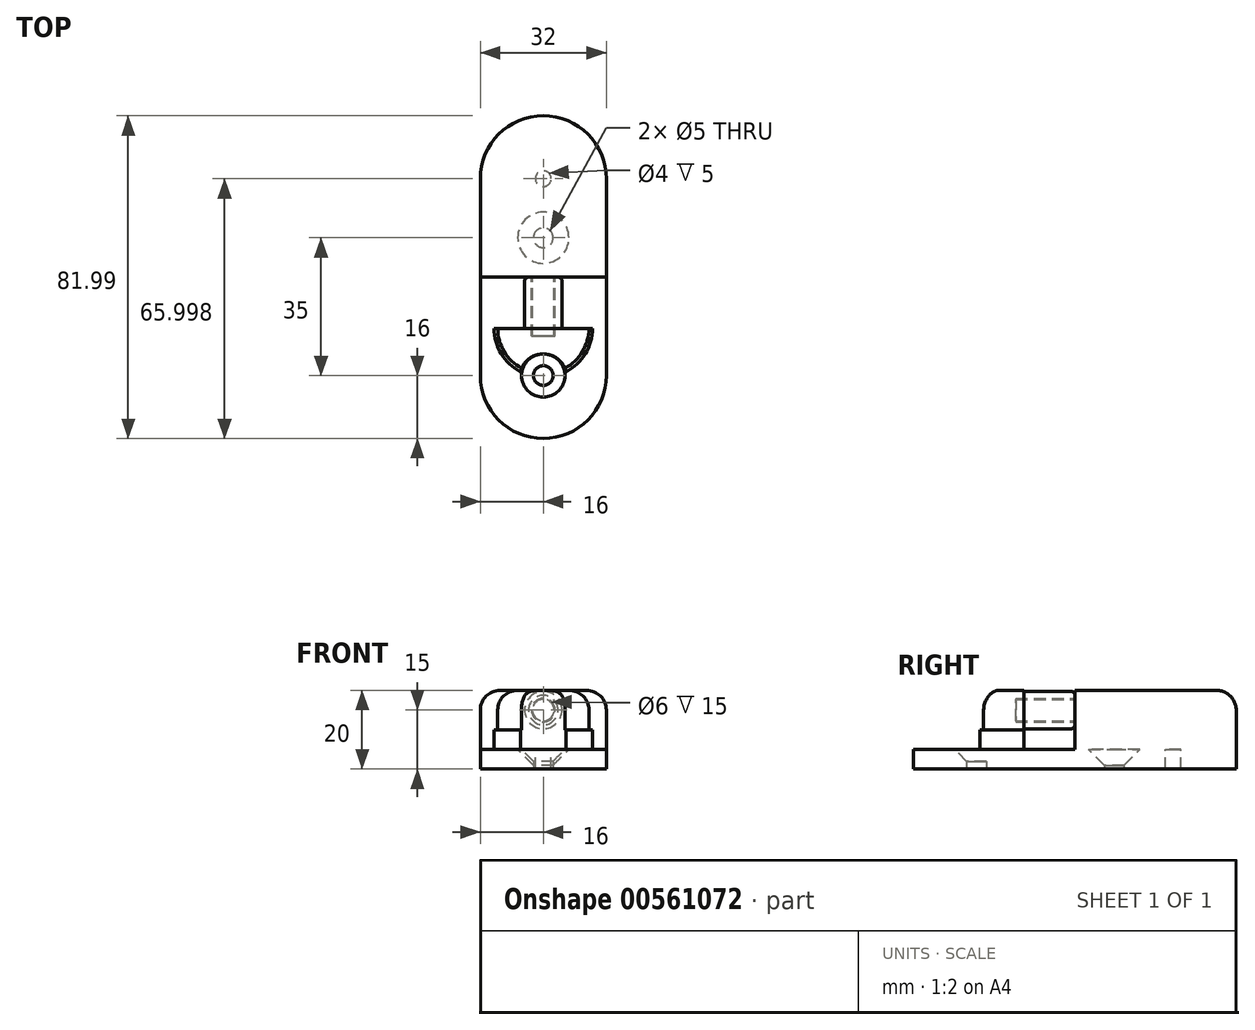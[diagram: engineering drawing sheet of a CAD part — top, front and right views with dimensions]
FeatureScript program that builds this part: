
annotation { "Feature Type Name" : "Feature", "Feature Type Description" : "" }
export const myFeature = defineFeature(function(context is Context, id is Id, definition is map)
    precondition{}
    {
        {
            var Q0;
            Q0=qCreatedBy(makeId("Top.planeOp"),FACE);
            var sketch = newSketch(context, id + "F0", { "sketchPlane" : qUnion([Q0])});
            skCircle(sketch, "E0", {"center": v(0, 17.5) * mm, "radius": 2.5 * mm});
            skCircle(sketch, "E1.MirrorC", {"center": v(0, -17.5) * mm, "radius": 2.5 * mm});
            skArc(sketch, "E2", {"start": v(-16, -17.5) * mm, "mid": v(0, -33.5) * mm, "end": v(16, -17.5) * mm});
            skLineSegment(sketch, "E3", {"start": v(-16, -5.5) * mm, "end": v(-12.5, -5.5) * mm});
            skLineSegment(sketch, "E4", {"start": v(16, -17.5) * mm, "end": v(16, -5.5) * mm});
            skLineSegment(sketch, "E5", {"start": v(-16, -17.5) * mm, "end": v(-16, -5.5) * mm});
            skLineSegment(sketch, "E6", {"start": v(-12.5, -5.5) * mm, "end": v(-12.5, 24.5) * mm});
            skLineSegment(sketch, "E7.MirrorCS", {"start": v(12.5, -5.5) * mm, "end": v(12.5, 24.5) * mm});
            skLineSegment(sketch, "E8", {"start": v(-12.5, 24.5) * mm, "end": v(-5, 24.5) * mm});
            skLineSegment(sketch, "E9", {"start": v(-5, 24.5) * mm, "end": v(-5, 36.5) * mm});
            skLineSegment(sketch, "E10.MirrorCS", {"start": v(5, 24.5) * mm, "end": v(5, 36.5) * mm});
            skLineSegment(sketch, "E11", {"start": v(-5, 36.5) * mm, "end": v(5, 36.5) * mm});
            skLineSegment(sketch, "E12.trimOffspring", {"start": v(5, 24.5) * mm, "end": v(12.5, 24.5) * mm});
            skLineSegment(sketch, "E13.trimOffspring", {"start": v(12.5, -5.5) * mm, "end": v(16, -5.5) * mm});
            skSolve(sketch);
        }
        {
            var Q0;
            Q0=makeQuery(id+"F0.imprint","IMPRINT",FACE,{"disambiguationData":[TD([[makeQuery(id+"F0.imprint","IMPRINT",EDGE,{"derivedFrom":sQuery(id+"F0.wireOp",EDGE,"E0")}),-1.0]])]});
            extrude(context, id + "F1", {"entities" : qUnion([Q0]), "depth" : 5 * mm, "offsetDistance" : 25 * mm});
        }
        {
            var Q0;
            Q0=makeQuery(id+"F1.opExtrude","CAP_EDGE",EDGE,{"disambiguationData":[OSD([sQuery(id+"F0.wireOp",EDGE,"E0")])],"isStart":false});
            chamfer(context, id + "F2", {"entities" : qUnion([Q0]), "width" : 4 * mm, "tangentPropagation" : true});
        }
        {
            var Q0;
            Q0=makeQuery(id+"F1.opExtrude","CAP_EDGE",EDGE,{"disambiguationData":[OSD([sQuery(id+"F0.wireOp",EDGE,"E1.MirrorC")])],"isStart":false});
            chamfer(context, id + "F3", {"entities" : qUnion([Q0]), "width" : 3 * mm, "tangentPropagation" : true});
        }
        {
            var Q0;
            Q0=makeQuery(id+"F1.opExtrude","CAP_FACE",FACE,{"disambiguationData":[OSD([sQuery(id+"F0.wireOp",EDGE,"E0"),sQuery(id+"F0.wireOp",EDGE,"E1.MirrorC"),sQuery(id+"F0.wireOp",EDGE,"E2"),sQuery(id+"F0.wireOp",EDGE,"E3"),sQuery(id+"F0.wireOp",EDGE,"E4"),sQuery(id+"F0.wireOp",EDGE,"E5"),sQuery(id+"F0.wireOp",EDGE,"E6"),sQuery(id+"F0.wireOp",EDGE,"E7.MirrorCS"),sQuery(id+"F0.wireOp",EDGE,"E8"),sQuery(id+"F0.wireOp",EDGE,"E9"),sQuery(id+"F0.wireOp",EDGE,"E10.MirrorCS"),sQuery(id+"F0.wireOp",EDGE,"E11"),sQuery(id+"F0.wireOp",EDGE,"E12.trimOffspring"),sQuery(id+"F0.wireOp",EDGE,"E13.trimOffspring")])],"isStart":false});
            var sketch = newSketch(context, id + "F4", { "sketchPlane" : qUnion([Q0])});
            skLineSegment(sketch, "E14", {"start": v(-12.5, -5.5) * mm, "end": v(12.5, -5.5) * mm});
            skArc(sketch, "E15", {"start": v(-12.5, -5.5) * mm, "mid": v(-10.7, -11.96) * mm, "end": v(-5.82, -16.56) * mm});
            skArc(sketch, "E16", {"start": v(5.82, -16.56) * mm, "mid": v(0, -12) * mm, "end": v(-5.82, -16.56) * mm});
            skArc(sketch, "E17.trimOffspring", {"start": v(5.82, -16.56) * mm, "mid": v(10.7, -11.96) * mm, "end": v(12.5, -5.5) * mm});
            skSolve(sketch);
        }
        {
            var Q0;
            Q0=makeQuery(id+"F4.imprint","IMPRINT",FACE,{"disambiguationData":[TD([[makeQuery(id+"F4.imprint","IMPRINT",EDGE,{"derivedFrom":sQuery(id+"F4.wireOp",EDGE,"E14")}),-1.0]])]});
            extrude(context, id + "F5", {"entities" : qUnion([Q0]), "operationType" : NewBodyOperationType.ADD, "depth" : 5 * mm, "offsetDistance" : 25 * mm});
        }
        {
            var Q0;
            Q0=makeQuery(id+"F5.opExtrude","CAP_FACE",FACE,{"disambiguationData":[OSD([sQuery(id+"F4.wireOp",EDGE,"E14"),sQuery(id+"F4.wireOp",EDGE,"E15"),sQuery(id+"F4.wireOp",EDGE,"E16"),sQuery(id+"F4.wireOp",EDGE,"E17.trimOffspring")])],"isStart":false});
            var sketch = newSketch(context, id + "F6", { "sketchPlane" : qUnion([Q0])});
            skArc(sketch, "E18", {"start": v(-11.58, -5.5) * mm, "mid": v(-9.95, -11.42) * mm, "end": v(-5.53, -15.68) * mm});
            skLineSegment(sketch, "E19", {"start": v(-11.58, -5.5) * mm, "end": v(11.58, -5.5) * mm});
            skArc(sketch, "E20", {"start": v(5.53, -15.68) * mm, "mid": v(0, -12) * mm, "end": v(-5.53, -15.68) * mm});
            skArc(sketch, "E21.trimOffspring", {"start": v(5.53, -15.68) * mm, "mid": v(9.95, -11.42) * mm, "end": v(11.58, -5.5) * mm});
            skSolve(sketch);
        }
        {
            var Q0;
            Q0=makeQuery(id+"F6.imprint","IMPRINT",FACE,{"disambiguationData":[TD([[makeQuery(id+"F6.imprint","IMPRINT",EDGE,{"derivedFrom":sQuery(id+"F6.wireOp",EDGE,"E18")}),1.0]])]});
            extrude(context, id + "F7", {"entities" : qUnion([Q0]), "operationType" : NewBodyOperationType.ADD, "depth" : 10 * mm, "offsetDistance" : 25 * mm});
        }
        {
            var Q0;
            Q0=makeQuery(id+"F7.boolean.opBoolean","MERGE",FACE,{"derivedFrom":[makeQuery(id+"F5.opExtrude","SWEPT_FACE",FACE,{"disambiguationData":[OSD([sQuery(id+"F4.wireOp",EDGE,"E14")])]}),makeQuery(id+"F7.opExtrude","SWEPT_FACE",FACE,{"disambiguationData":[OSD([sQuery(id+"F6.wireOp",EDGE,"E19")])]})]});
            var sketch = newSketch(context, id + "F8", { "sketchPlane" : qUnion([Q0])});
            skCircle(sketch, "E22", {"center": v(0, 15) * mm, "radius": 4.75 * mm});
            skSolve(sketch);
        }
        {
            var Q0;
            Q0=makeQuery(id+"F8.imprint","IMPRINT",FACE,{"disambiguationData":[TD([[makeQuery(id+"F8.imprint","IMPRINT",EDGE,{"derivedFrom":sQuery(id+"F8.wireOp",EDGE,"E22")}),1.0]])]});
            extrude(context, id + "F9", {"entities" : qUnion([Q0]), "operationType" : NewBodyOperationType.ADD, "depth" : 13 * mm, "offsetDistance" : 25 * mm});
        }
        {
            var Q0;
            Q0=makeQuery(id+"F9.opExtrude","CAP_EDGE",EDGE,{"disambiguationData":[OSD([sQuery(id+"F8.wireOp",EDGE,"E22")])],"isStart":false});
            fillet(context, id + "F10", {"entities" : qUnion([Q0]), "radius" : 1 * mm, "tangentPropagation" : true, "allowEdgeOverflow" : false});
        }
        {
            var Q0;
            Q0=makeQuery(id+"F7.opExtrude","CAP_EDGE",EDGE,{"disambiguationData":[OSD([sQuery(id+"F6.wireOp",EDGE,"E21.trimOffspring")])],"isStart":false});
            var Q1;
            Q1=makeQuery(id+"F7.opExtrude","CAP_EDGE",EDGE,{"disambiguationData":[OSD([sQuery(id+"F6.wireOp",EDGE,"E18")])],"isStart":false});
            fillet(context, id + "F11", {"entities" : qUnion([Q0, Q1]), "radius" : 5 * mm, "tangentPropagation" : true, "allowEdgeOverflow" : false});
        }
        {
            var Q0;
            Q0=makeQuery(id+"F1.opExtrude","CAP_EDGE",EDGE,{"disambiguationData":[OSD([sQuery(id+"F0.wireOp",EDGE,"E7.MirrorCS")])],"isStart":true});
            var Q1;
            Q1=makeQuery(id+"F1.opExtrude","CAP_EDGE",EDGE,{"disambiguationData":[OSD([sQuery(id+"F0.wireOp",EDGE,"E6")])],"isStart":true});
            chamfer(context, id + "F12", {"entities" : qUnion([Q0, Q1]), "chamferType" : ChamferType.TWO_OFFSETS, "width1" : 5 * mm, "oppositeDirection" : false, "width2" : 3 * mm, "tangentPropagation" : true});
        }
        {
            var Q0;
            {var subQ0=sQuery(id+"F0.wireOp",EDGE,"E13.trimOffspring");var subQ1=sQuery(id+"F0.wireOp",EDGE,"E12.trimOffspring");var subQ2=sQuery(id+"F0.wireOp",EDGE,"E10.MirrorCS");var subQ3=sQuery(id+"F0.wireOp",EDGE,"E9");var subQ4=sQuery(id+"F0.wireOp",EDGE,"E8");var subQ5=sQuery(id+"F0.wireOp",EDGE,"E11");var subQ6=sQuery(id+"F0.wireOp",EDGE,"E7.MirrorCS");var subQ7=sQuery(id+"F0.wireOp",EDGE,"E6");var subQ8=sQuery(id+"F0.wireOp",EDGE,"E3");var subQ9=sQuery(id+"F0.wireOp",EDGE,"E0");var subQ10=makeQuery(id+"F1.opExtrude","CAP_FACE",FACE,{"disambiguationData":[OSD([subQ9,sQuery(id+"F0.wireOp",EDGE,"E1.MirrorC"),sQuery(id+"F0.wireOp",EDGE,"E2"),subQ8,sQuery(id+"F0.wireOp",EDGE,"E4"),sQuery(id+"F0.wireOp",EDGE,"E5"),subQ7,subQ6,subQ4,subQ3,subQ2,subQ5,subQ1,subQ0])],"isStart":false});Q0=makeQuery(id+"F5.boolean.opBoolean","SPLIT",FACE,{"disambiguationData":[TD([makeQuery(id+"F1.opExtrude","SWEPT_FACE",FACE,{"disambiguationData":[OSD([subQ4])]})])],"derivedFrom":subQ10});}
            var sketch = newSketch(context, id + "F13", { "sketchPlane" : qUnion([Q0])});
            skCircle(sketch, "E23", {"center": v(0, 32.5) * mm, "radius": 2 * mm});
            skSolve(sketch);
        }
        {
            var Q0;
            Q0=makeQuery(id+"F13.imprint","IMPRINT",FACE,{"disambiguationData":[TD([[makeQuery(id+"F13.imprint","IMPRINT",EDGE,{"derivedFrom":sQuery(id+"F13.wireOp",EDGE,"E23")}),1.0]])]});
            extrude(context, id + "F14", {"entities" : qUnion([Q0]), "operationType" : NewBodyOperationType.REMOVE, "oppositeDirection" : true, "depth" : 25 * mm, "offsetDistance" : 25 * mm});
        }
        {
            var Q0;
            Q0=makeQuery(id+"F9.opExtrude","CAP_FACE",FACE,{"disambiguationData":[OSD([sQuery(id+"F8.wireOp",EDGE,"E22")])],"isStart":false});
            var sketch = newSketch(context, id + "F15", { "sketchPlane" : qUnion([Q0])});
            skCircle(sketch, "E24", {"center": v(0, 15) * mm, "radius": 3 * mm});
            skSolve(sketch);
        }
        {
            var Q0;
            Q0=makeQuery(id+"F15.imprint","IMPRINT",FACE,{"disambiguationData":[TD([[makeQuery(id+"F15.imprint","IMPRINT",EDGE,{"derivedFrom":sQuery(id+"F15.wireOp",EDGE,"E24")}),1.0]])]});
            extrude(context, id + "F16", {"entities" : qUnion([Q0]), "operationType" : NewBodyOperationType.REMOVE, "oppositeDirection" : true, "depth" : 15 * mm, "offsetDistance" : 25 * mm});
        }
        {
            var Q0;
            Q0=makeQuery(id+"F1.opExtrude","SWEPT_FACE",FACE,{"disambiguationData":[OSD([sQuery(id+"F0.wireOp",EDGE,"E13.trimOffspring")])]});
            var sketch = newSketch(context, id + "F17", { "sketchPlane" : qUnion([Q0])});
            skLineSegment(sketch, "E25", {"start": v(-12.5, 5) * mm, "end": v(-9.5, 0) * mm});
            skLineSegment(sketch, "E26", {"start": v(-9.5, 0) * mm, "end": v(-16, 0) * mm});
            skLineSegment(sketch, "E27", {"start": v(-16, 0) * mm, "end": v(-16, 5) * mm});
            skLineSegment(sketch, "E28", {"start": v(-16, 5) * mm, "end": v(-12.5, 5) * mm});
            skPoint(sketch, "E29.start.orphan", {"position": v(16.1, 0) * mm});
            skLineSegment(sketch, "E30.MirrorCS", {"start": v(12.5, 5) * mm, "end": v(9.5, 0) * mm});
            skLineSegment(sketch, "E31.MirrorCS", {"start": v(16, 5) * mm, "end": v(12.5, 5) * mm});
            skLineSegment(sketch, "E32.MirrorCS", {"start": v(16, 0) * mm, "end": v(16, 5) * mm});
            skLineSegment(sketch, "E33.MirrorCS", {"start": v(9.5, 0) * mm, "end": v(16, 0) * mm});
            skSolve(sketch);
        }
        {
            var Q0;
            Q0=makeQuery(id+"F17.imprint","IMPRINT",FACE,{"disambiguationData":[TD([[makeQuery(id+"F17.imprint","IMPRINT",EDGE,{"derivedFrom":sQuery(id+"F17.wireOp",EDGE,"E30.MirrorCS")}),1.0]])]});
            var Q1;
            Q1=makeQuery(id+"F17.imprint","IMPRINT",FACE,{"disambiguationData":[TD([[makeQuery(id+"F17.imprint","IMPRINT",EDGE,{"derivedFrom":sQuery(id+"F17.wireOp",EDGE,"E25")}),1.0]])]});
            var Q2;
            Q2=makeQuery(id+"F1.opExtrude","SWEPT_FACE",FACE,{"disambiguationData":[OSD([sQuery(id+"F0.wireOp",EDGE,"E12.trimOffspring")])]});
            extrude(context, id + "F18", {"entities" : qUnion([Q0, Q1]), "endBound" : BoundingType.UP_TO_SURFACE, "depth" : 25 * mm, "endBoundEntityFace" : qUnion([Q2]), "offsetDistance" : 25 * mm});
        }
        {
            var Q0;
            Q0=qCreatedBy(makeId("Top.planeOp"),FACE);
            var sketch = newSketch(context, id + "F19", { "sketchPlane" : qUnion([Q0])});
            skArc(sketch, "E34", {"start": v(16, 32.49) * mm, "mid": v(0, 48.49) * mm, "end": v(-16, 32.49) * mm});
            skPoint(sketch, "E35.0", {"position": v(0, 36.5) * mm});
            skLineSegment(sketch, "E36.0", {"start": v(-5, 36.5) * mm, "end": v(5, 36.5) * mm});
            skLineSegment(sketch, "E37.0", {"start": v(-5, 32.49) * mm, "end": v(-5, 36.5) * mm});
            skLineSegment(sketch, "E38.0", {"start": v(5, 32.49) * mm, "end": v(5, 36.5) * mm});
            skLineSegment(sketch, "E39.0", {"start": v(12.5, 24.5) * mm, "end": v(16, 24.5) * mm});
            skLineSegment(sketch, "E40.0", {"start": v(-16, 24.5) * mm, "end": v(-12.5, 24.5) * mm});
            skLineSegment(sketch, "E41.0", {"start": v(-16, 24.5) * mm, "end": v(-16, -5.5) * mm});
            skLineSegment(sketch, "E42.0", {"start": v(16, 24.5) * mm, "end": v(16, -5.5) * mm});
            skLineSegment(sketch, "E43", {"start": v(-16, 32.49) * mm, "end": v(-16, 24.5) * mm});
            skLineSegment(sketch, "E44", {"start": v(16, 32.49) * mm, "end": v(16, 24.5) * mm});
            skPoint(sketch, "E45.orphan", {"position": v(-5, 24.5) * mm});
            skPoint(sketch, "E46.orphan", {"position": v(5, 24.5) * mm});
            skLineSegment(sketch, "E47", {"start": v(5, 32.49) * mm, "end": v(5, 24.5) * mm});
            skLineSegment(sketch, "E48", {"start": v(12.5, 24.5) * mm, "end": v(5, 24.5) * mm});
            skLineSegment(sketch, "E49", {"start": v(-5, 24.5) * mm, "end": v(-12.5, 24.5) * mm});
            skLineSegment(sketch, "E50", {"start": v(-5, 32.49) * mm, "end": v(-5, 24.5) * mm});
            skSolve(sketch);
        }
        {
            var Q0;
            Q0=makeQuery(id+"F19.imprint","IMPRINT",FACE,{"disambiguationData":[TD([[makeQuery(id+"F19.imprint","IMPRINT",EDGE,{"derivedFrom":sQuery(id+"F19.wireOp",EDGE,"E34")}),1.0]])]});
            var Q1;
            Q1=makeQuery(id+"F7.opExtrude","CAP_FACE",FACE,{"disambiguationData":[OSD([sQuery(id+"F6.wireOp",EDGE,"E18"),sQuery(id+"F6.wireOp",EDGE,"E19"),sQuery(id+"F6.wireOp",EDGE,"E20"),sQuery(id+"F6.wireOp",EDGE,"E21.trimOffspring")])],"isStart":false});
            extrude(context, id + "F20", {"entities" : qUnion([Q0]), "operationType" : NewBodyOperationType.ADD, "endBound" : BoundingType.UP_TO_SURFACE, "depth" : 25 * mm, "endBoundEntityFace" : qUnion([Q1]), "offsetDistance" : 25 * mm});
        }
        {
            var Q0;
            Q0=makeQuery(id+"F20.opExtrude","SWEPT_FACE",FACE,{"disambiguationData":[OSD([sQuery(id+"F19.wireOp",EDGE,"E36.0")])]});
            var sketch = newSketch(context, id + "F21", { "sketchPlane" : qUnion([Q0])});
            skLineSegment(sketch, "E51.0", {"start": v(-5, 5) * mm, "end": v(5, 5) * mm});
            skPoint(sketch, "E52.0", {"position": v(5, 10) * mm});
            skLineSegment(sketch, "E53.0", {"start": v(5, 20) * mm, "end": v(5, 5) * mm});
            skLineSegment(sketch, "E54.0", {"start": v(-5, 20) * mm, "end": v(-5, 5) * mm});
            skLineSegment(sketch, "E55.0", {"start": v(-5, 20) * mm, "end": v(5, 20) * mm});
            skPoint(sketch, "E56.orphan", {"position": v(-5, 0) * mm});
            skPoint(sketch, "E57.orphan", {"position": v(5, 0) * mm});
            skSolve(sketch);
        }
        {
            var Q0;
            Q0=makeQuery(id+"F21.imprint","IMPRINT",FACE,{"disambiguationData":[TD([[makeQuery(id+"F21.imprint","IMPRINT",EDGE,{"derivedFrom":sQuery(id+"F21.wireOp",EDGE,"E51.0")}),1.0]])]});
            var Q1;
            Q1=makeQuery(id+"F9.opExtrude","CAP_FACE",FACE,{"disambiguationData":[OSD([sQuery(id+"F8.wireOp",EDGE,"E22")])],"isStart":false});
            extrude(context, id + "F22", {"entities" : qUnion([Q0]), "operationType" : NewBodyOperationType.ADD, "endBound" : BoundingType.UP_TO_SURFACE, "depth" : 25 * mm, "endBoundEntityFace" : qUnion([Q1]), "offsetDistance" : 25 * mm});
        }
        {
            var Q0;
            {var subQ0=sQuery(id+"F0.wireOp",EDGE,"E13.trimOffspring");var subQ1=sQuery(id+"F0.wireOp",EDGE,"E12.trimOffspring");var subQ2=sQuery(id+"F0.wireOp",EDGE,"E10.MirrorCS");var subQ3=sQuery(id+"F0.wireOp",EDGE,"E9");var subQ4=sQuery(id+"F0.wireOp",EDGE,"E8");var subQ5=sQuery(id+"F0.wireOp",EDGE,"E11");var subQ6=sQuery(id+"F0.wireOp",EDGE,"E7.MirrorCS");var subQ7=sQuery(id+"F0.wireOp",EDGE,"E6");var subQ8=sQuery(id+"F0.wireOp",EDGE,"E3");var subQ9=sQuery(id+"F0.wireOp",EDGE,"E0");var subQ10=makeQuery(id+"F1.opExtrude","CAP_FACE",FACE,{"disambiguationData":[OSD([subQ9,sQuery(id+"F0.wireOp",EDGE,"E1.MirrorC"),sQuery(id+"F0.wireOp",EDGE,"E2"),subQ8,sQuery(id+"F0.wireOp",EDGE,"E4"),sQuery(id+"F0.wireOp",EDGE,"E5"),subQ7,subQ6,subQ4,subQ3,subQ2,subQ5,subQ1,subQ0])],"isStart":false});Q0=makeQuery(id+"F5.boolean.opBoolean","SPLIT",FACE,{"disambiguationData":[TD([makeQuery(id+"F1.opExtrude","SWEPT_FACE",FACE,{"disambiguationData":[OSD([subQ4])]})])],"derivedFrom":subQ10});}
            var sketch = newSketch(context, id + "F23", { "sketchPlane" : qUnion([Q0])});
            skLineSegment(sketch, "E58.0", {"start": v(5, 7.5) * mm, "end": v(5, 24.5) * mm});
            skLineSegment(sketch, "E59.0", {"start": v(16, 24.5) * mm, "end": v(16, 7.5) * mm});
            skLineSegment(sketch, "E60", {"start": v(5, 7.5) * mm, "end": v(16, 7.5) * mm});
            skLineSegment(sketch, "E61", {"start": v(5, 24.5) * mm, "end": v(16, 24.5) * mm});
            skLineSegment(sketch, "E62.MirrorCS", {"start": v(-5, 24.5) * mm, "end": v(-6, 24.5) * mm});
            skLineSegment(sketch, "E63.MirrorCS", {"start": v(-5, 24.5) * mm, "end": v(-16, 24.5) * mm});
            skLineSegment(sketch, "E64.MirrorCS", {"start": v(-5, 7.5) * mm, "end": v(-5, 24.5) * mm});
            skLineSegment(sketch, "E65.MirrorCS", {"start": v(-5, 7.5) * mm, "end": v(-16, 7.5) * mm});
            skLineSegment(sketch, "E66.MirrorCS", {"start": v(-16, 24.5) * mm, "end": v(-16, 7.5) * mm});
            skPoint(sketch, "E67.orphan", {"position": v(-16, -5.5) * mm});
            skPoint(sketch, "E68.orphan", {"position": v(16, -5.5) * mm});
            skPoint(sketch, "E69.0.end.orphan", {"position": v(-5, 7.5) * mm});
            skPoint(sketch, "E69.0.start.orphan", {"position": v(5, 7.5) * mm});
            skPoint(sketch, "E70.orphan", {"position": v(5, 24.5) * mm});
            skSolve(sketch);
        }
        {
            var Q0;
            Q0 = qSketchRegion(id + "F23", true);
            var Q1;
            Q1=makeQuery(id+"F22.boolean.opBoolean","MERGE",FACE,{"derivedFrom":[makeQuery(id+"F20.opExtrude","CAP_FACE",FACE,{"disambiguationData":[OSD([sQuery(id+"F19.wireOp",EDGE,"E34"),sQuery(id+"F19.wireOp",EDGE,"E36.0"),sQuery(id+"F19.wireOp",EDGE,"E37.0"),sQuery(id+"F19.wireOp",EDGE,"E38.0"),sQuery(id+"F19.wireOp",EDGE,"E39.0"),sQuery(id+"F19.wireOp",EDGE,"E40.0"),sQuery(id+"F19.wireOp",EDGE,"E43"),sQuery(id+"F19.wireOp",EDGE,"E44"),sQuery(id+"F19.wireOp",EDGE,"E47"),sQuery(id+"F19.wireOp",EDGE,"E48"),sQuery(id+"F19.wireOp",EDGE,"E49"),sQuery(id+"F19.wireOp",EDGE,"E50")])],"isStart":false}),makeQuery(id+"F22.opExtrude","SWEPT_FACE",FACE,{"disambiguationData":[OSD([sQuery(id+"F21.wireOp",EDGE,"E55.0")])]})]});
            extrude(context, id + "F24", {"entities" : qUnion([Q0]), "operationType" : NewBodyOperationType.ADD, "endBound" : BoundingType.UP_TO_SURFACE, "depth" : 25 * mm, "endBoundEntityFace" : qUnion([Q1]), "offsetDistance" : 25 * mm});
        }
        {
            var Q0;
            Q0=makeQuery(id+"F24.boolean.opBoolean","MERGE",EDGE,{"derivedFrom":[makeQuery(id+"F20.opExtrude","CAP_EDGE",EDGE,{"disambiguationData":[OSD([sQuery(id+"F19.wireOp",EDGE,"E44")])],"isStart":false}),makeQuery(id+"F24.opExtrude","CAP_EDGE",EDGE,{"disambiguationData":[OSD([sQuery(id+"F23.wireOp",EDGE,"E59.0")])],"isStart":false})]});
            fillet(context, id + "F25", {"entities" : qUnion([Q0]), "radius" : 5 * mm, "tangentPropagation" : true, "allowEdgeOverflow" : false});
        }
        {
            var Q0;
            Q0=makeQuery(id+"F24.boolean.opBoolean","MERGE",FACE,{"derivedFrom":[makeQuery(id+"F22.opExtrude","CAP_FACE",FACE,{"disambiguationData":[OSD([sQuery(id+"F21.wireOp",EDGE,"E51.0"),sQuery(id+"F21.wireOp",EDGE,"E53.0"),sQuery(id+"F21.wireOp",EDGE,"E54.0"),sQuery(id+"F21.wireOp",EDGE,"E55.0")])],"isStart":false}),makeQuery(id+"F24.opExtrude","SWEPT_FACE",FACE,{"disambiguationData":[OSD([sQuery(id+"F23.wireOp",EDGE,"E60")])]}),makeQuery(id+"F24.opExtrude","SWEPT_FACE",FACE,{"disambiguationData":[OSD([sQuery(id+"F23.wireOp",EDGE,"E65.MirrorCS")])]})]});
            var sketch = newSketch(context, id + "F26", { "sketchPlane" : qUnion([Q0])});
            skCircle(sketch, "E71", {"center": v(0, 15) * mm, "radius": 2.75 * mm});
            skSolve(sketch);
        }
        {
            var Q0;
            Q0 = qSketchRegion(id + "F26", true);
            extrude(context, id + "F27", {"entities" : qUnion([Q0]), "operationType" : NewBodyOperationType.ADD, "depth" : 15 * mm, "offsetDistance" : 25 * mm});
        }
    });
